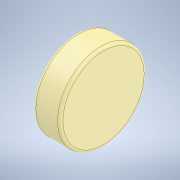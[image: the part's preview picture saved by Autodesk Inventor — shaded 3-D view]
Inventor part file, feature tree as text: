
AUTODESK INVENTOR PART (.ipt)
format: ipt  version: 2022.1 (Build 261234000, 234)  size: 118,272 bytes
history: native  units: mm
features: other x1, extrude x1, fillet x1, sketch x1
ambient origin geometry x8: Origin, YZ Plane, XZ Plane, XY Plane, X Axis, Y Axis, Z Axis, Center Point
bodies: Body1 (feature_tree)
feature tree (4):
  other  "Sólido1"
  extrude  "Extrusión1"  Depth=50.0mm TaperAngle=0.0deg
  fillet  "Empalme1"  Radius=5.0mm
  sketch  "Boceto1"  dims[d0=160.0mm d1=50.0mm d2=0.0mm d3=5.0mm]
